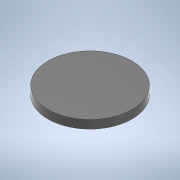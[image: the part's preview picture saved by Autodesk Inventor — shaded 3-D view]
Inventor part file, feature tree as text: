
AUTODESK INVENTOR PART (.ipt)
format: ipt  version: 2020 (Build 240168000, 168)  size: 95,232 bytes
history: native  units: mm
features: other x1, extrude x1, sketch x1
ambient origin geometry x8: Origin, YZ Plane, XZ Plane, XY Plane, X Axis, Y Axis, Z Axis, Center Point
bodies: Body1 (feature_tree)
feature tree (3):
  other  "Твердое тело1"
  extrude  "Выдавливание1"  Depth=50.0mm
  sketch  "Эскиз1"
